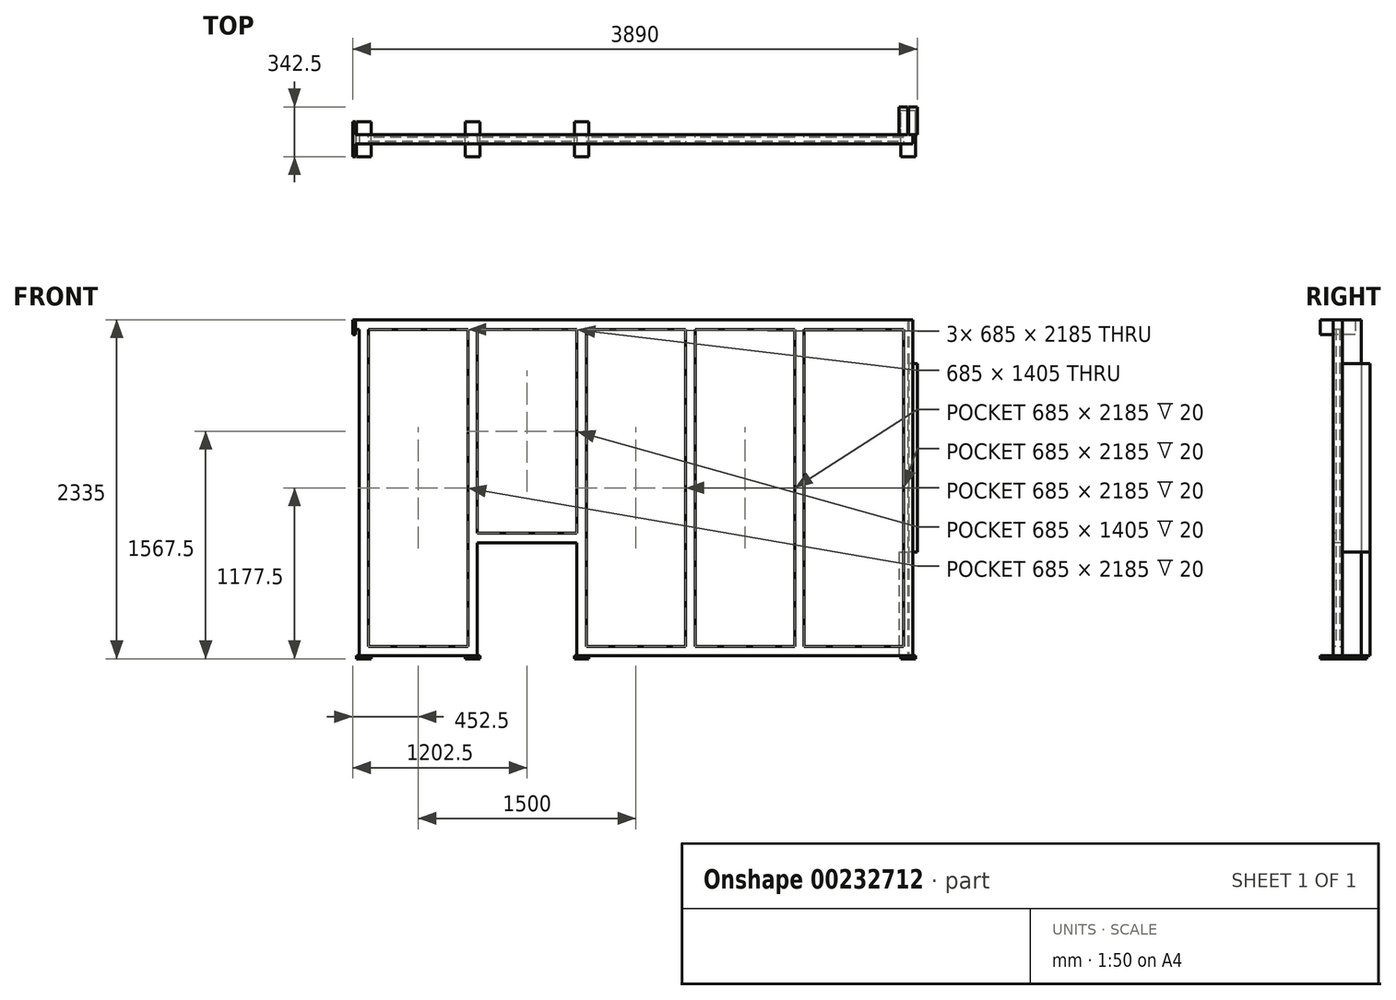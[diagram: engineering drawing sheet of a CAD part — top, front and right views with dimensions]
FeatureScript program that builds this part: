
annotation { "Feature Type Name" : "Feature", "Feature Type Description" : "" }
export const myFeature = defineFeature(function(context is Context, id is Id, definition is map)
    precondition{}
    {
        {
            var Q0;
            Q0=qCreatedBy(makeId("Front.planeOp"),FACE);
            var sketch = newSketch(context, id + "F0", { "sketchPlane" : qUnion([Q0])});
            skLineSegment(sketch, "E0.bottom", {"start": v(0, 0) * mm, "end": v(3815, 0) * mm});
            skLineSegment(sketch, "E0.top", {"start": v(0, 2315) * mm, "end": v(3815, 2315) * mm});
            skLineSegment(sketch, "E0.left", {"start": v(0, 0) * mm, "end": v(0, 2315) * mm});
            skLineSegment(sketch, "E0.right", {"start": v(3815, 0) * mm, "end": v(3815, 2315) * mm});
            skSolve(sketch);
        }
        {
            var Q0;
            Q0 = qSketchRegion(id + "F0", true);
            extrude(context, id + "F1", {"entities" : qUnion([Q0]), "oppositeDirection" : true, "depth" : 65 * mm});
        }
        {
            var Q0;
            Q0=makeQuery(id+"F1.opExtrude","CAP_FACE",FACE,{"disambiguationData":[OSD([sQuery(id+"F0.wireOp",EDGE,"E0.bottom"),sQuery(id+"F0.wireOp",EDGE,"E0.top"),sQuery(id+"F0.wireOp",EDGE,"E0.left"),sQuery(id+"F0.wireOp",EDGE,"E0.right")])],"isStart":true});
            var sketch = newSketch(context, id + "F2", { "sketchPlane" : qUnion([Q0])});
            skLineSegment(sketch, "E1.bottom", {"start": v(65, 65) * mm, "end": v(750, 65) * mm});
            skLineSegment(sketch, "E1.top", {"start": v(65, 2250) * mm, "end": v(750, 2250) * mm});
            skLineSegment(sketch, "E1.left", {"start": v(65, 65) * mm, "end": v(65, 2250) * mm});
            skLineSegment(sketch, "E1.right", {"start": v(750, 65) * mm, "end": v(750, 2250) * mm});
            skLineSegment(sketch, "E2.bottom", {"start": v(815, 2250) * mm, "end": v(1500, 2250) * mm});
            skLineSegment(sketch, "E2.top", {"start": v(815, 845) * mm, "end": v(1500, 845) * mm});
            skLineSegment(sketch, "E2.left", {"start": v(815, 2250) * mm, "end": v(815, 845) * mm});
            skLineSegment(sketch, "E2.right", {"start": v(1500, 2250) * mm, "end": v(1500, 845) * mm});
            skLineSegment(sketch, "E3.bottom", {"start": v(1565, 2250) * mm, "end": v(2250, 2250) * mm});
            skLineSegment(sketch, "E3.top", {"start": v(1565, 65) * mm, "end": v(2250, 65) * mm});
            skLineSegment(sketch, "E3.left", {"start": v(1565, 2250) * mm, "end": v(1565, 65) * mm});
            skLineSegment(sketch, "E3.right", {"start": v(2250, 2250) * mm, "end": v(2250, 65) * mm});
            skLineSegment(sketch, "E4.bottom", {"start": v(3065, 2250) * mm, "end": v(3750, 2250) * mm});
            skLineSegment(sketch, "E4.top", {"start": v(3065, 65) * mm, "end": v(3750, 65) * mm});
            skLineSegment(sketch, "E4.left", {"start": v(3065, 2250) * mm, "end": v(3065, 65) * mm});
            skLineSegment(sketch, "E4.right", {"start": v(3750, 2250) * mm, "end": v(3750, 65) * mm});
            skLineSegment(sketch, "E5.bottom", {"start": v(2315, 2250) * mm, "end": v(3000, 2250) * mm});
            skLineSegment(sketch, "E5.top", {"start": v(2315, 65) * mm, "end": v(3000, 65) * mm});
            skLineSegment(sketch, "E5.left", {"start": v(2315, 2250) * mm, "end": v(2315, 65) * mm});
            skLineSegment(sketch, "E5.right", {"start": v(3000, 2250) * mm, "end": v(3000, 65) * mm});
            skSolve(sketch);
        }
        {
            var Q0;
            Q0 = qSketchRegion(id + "F2", true);
            extrude(context, id + "F3", {"entities" : qUnion([Q0]), "operationType" : NewBodyOperationType.REMOVE, "oppositeDirection" : true, "depth" : 20 * mm});
        }
        {
            var Q0;
            {var subQ1=sQuery(id+"F0.wireOp",EDGE,"E0.left");var subQ3=sQuery(id+"F0.wireOp",EDGE,"E0.bottom");Q0=makeQuery(id+"F3.boolean.opBoolean","SPLIT",FACE,{"disambiguationData":[TD([makeQuery(id+"F1.opExtrude","SWEPT_FACE",FACE,{"disambiguationData":[OSD([subQ1])]})])],"derivedFrom":makeQuery(id+"F1.opExtrude","SWEPT_FACE",FACE,{"disambiguationData":[OSD([subQ3])]})});}
            var sketch = newSketch(context, id + "F4", { "sketchPlane" : qUnion([Q0])});
            skLineSegment(sketch, "E6.bottom", {"start": v(-17.5, 87.5) * mm, "end": v(82.5, 87.5) * mm});
            skLineSegment(sketch, "E6.top", {"start": v(-17.5, -152.5) * mm, "end": v(82.5, -152.5) * mm});
            skLineSegment(sketch, "E6.left", {"start": v(-17.5, 87.5) * mm, "end": v(-17.5, -152.5) * mm});
            skLineSegment(sketch, "E6.right", {"start": v(82.5, 87.5) * mm, "end": v(82.5, -152.5) * mm});
            skLineSegment(sketch, "E7.bottom", {"start": v(732.5, 87.5) * mm, "end": v(832.5, 87.5) * mm});
            skLineSegment(sketch, "E7.top", {"start": v(732.5, -152.5) * mm, "end": v(832.5, -152.5) * mm});
            skLineSegment(sketch, "E7.left", {"start": v(732.5, 87.5) * mm, "end": v(732.5, -152.5) * mm});
            skLineSegment(sketch, "E7.right", {"start": v(832.5, 87.5) * mm, "end": v(832.5, -152.5) * mm});
            skLineSegment(sketch, "E8.bottom", {"start": v(1482.5, 87.5) * mm, "end": v(1582.5, 87.5) * mm});
            skLineSegment(sketch, "E8.top", {"start": v(1482.5, -152.5) * mm, "end": v(1582.5, -152.5) * mm});
            skLineSegment(sketch, "E8.left", {"start": v(1482.5, 87.5) * mm, "end": v(1482.5, -152.5) * mm});
            skLineSegment(sketch, "E8.right", {"start": v(1582.5, 87.5) * mm, "end": v(1582.5, -152.5) * mm});
            skLineSegment(sketch, "E9.bottom", {"start": v(3732.5, 87.5) * mm, "end": v(3832.5, 87.5) * mm});
            skLineSegment(sketch, "E9.top", {"start": v(3732.5, -232.5) * mm, "end": v(3832.5, -232.5) * mm});
            skLineSegment(sketch, "E9.left", {"start": v(3732.5, 87.5) * mm, "end": v(3732.5, -232.5) * mm});
            skLineSegment(sketch, "E9.right", {"start": v(3832.5, 87.5) * mm, "end": v(3832.5, -232.5) * mm});
            skSolve(sketch);
        }
        {
            var Q0;
            Q0 = qSketchRegion(id + "F4", true);
            extrude(context, id + "F5", {"entities" : qUnion([Q0]), "operationType" : NewBodyOperationType.ADD, "depth" : 20 * mm});
        }
        {
            var Q0;
            Q0=makeQuery(id+"F1.opExtrude","SWEPT_FACE",FACE,{"disambiguationData":[OSD([sQuery(id+"F0.wireOp",EDGE,"E0.left")])]});
            var sketch = newSketch(context, id + "F6", { "sketchPlane" : qUnion([Q0])});
            skLineSegment(sketch, "E10.bottom", {"start": v(-65, 2315) * mm, "end": v(0, 2315) * mm});
            skLineSegment(sketch, "E10.top", {"start": v(-65, 2250) * mm, "end": v(0, 2250) * mm});
            skLineSegment(sketch, "E10.left", {"start": v(-65, 2315) * mm, "end": v(-65, 2250) * mm});
            skLineSegment(sketch, "E10.right", {"start": v(0, 2315) * mm, "end": v(0, 2250) * mm});
            skSolve(sketch);
        }
        {
            var Q0;
            Q0 = qSketchRegion(id + "F6", true);
            extrude(context, id + "F7", {"entities" : qUnion([Q0]), "operationType" : NewBodyOperationType.ADD, "depth" : 25 * mm});
        }
        {
            var Q0;
            Q0=makeQuery(id+"F7.opExtrude","CAP_FACE",FACE,{"disambiguationData":[OSD([sQuery(id+"F6.wireOp",EDGE,"E10.bottom"),sQuery(id+"F6.wireOp",EDGE,"E10.top"),sQuery(id+"F6.wireOp",EDGE,"E10.left"),sQuery(id+"F6.wireOp",EDGE,"E10.right")])],"isStart":false});
            var sketch = newSketch(context, id + "F8", { "sketchPlane" : qUnion([Q0])});
            skLineSegment(sketch, "E11.bottom", {"start": v(-152.5, 2315) * mm, "end": v(87.5, 2315) * mm});
            skLineSegment(sketch, "E11.top", {"start": v(-152.5, 2215) * mm, "end": v(87.5, 2215) * mm});
            skLineSegment(sketch, "E11.left", {"start": v(-152.5, 2315) * mm, "end": v(-152.5, 2215) * mm});
            skLineSegment(sketch, "E11.right", {"start": v(87.5, 2315) * mm, "end": v(87.5, 2215) * mm});
            skLineSegment(sketch, "E12", {"start": v(-32.5, 2315) * mm, "end": v(-32.5, 2215) * mm, "construction": true});
            skSolve(sketch);
        }
        {
            var Q0;
            Q0 = qSketchRegion(id + "F8", true);
            extrude(context, id + "F9", {"entities" : qUnion([Q0]), "operationType" : NewBodyOperationType.ADD, "depth" : 20 * mm});
        }
        {
            var Q0;
            Q0=makeQuery(id+"F7.boolean.opBoolean","MERGE",FACE,{"derivedFrom":[makeQuery(id+"F1.opExtrude","CAP_FACE",FACE,{"disambiguationData":[OSD([sQuery(id+"F0.wireOp",EDGE,"E0.bottom"),sQuery(id+"F0.wireOp",EDGE,"E0.top"),sQuery(id+"F0.wireOp",EDGE,"E0.left"),sQuery(id+"F0.wireOp",EDGE,"E0.right")])],"isStart":false}),makeQuery(id+"F7.opExtrude","SWEPT_FACE",FACE,{"disambiguationData":[OSD([sQuery(id+"F6.wireOp",EDGE,"E10.left")])]})]});
            var sketch = newSketch(context, id + "F10", { "sketchPlane" : qUnion([Q0])});
            skLineSegment(sketch, "E13.top", {"start": v(-3780, 0) * mm, "end": v(-3785, 0) * mm});
            skLineSegment(sketch, "E13.left", {"start": v(-3780, 2315) * mm, "end": v(-3780, 0) * mm});
            skLineSegment(sketch, "E13.right", {"start": v(-3785, 2315) * mm, "end": v(-3785, 0) * mm});
            skLineSegment(sketch, "E14", {"start": v(-3785, 2315) * mm, "end": v(-3780, 2315) * mm});
            skSolve(sketch);
        }
        {
            var Q0;
            Q0 = qSketchRegion(id + "F10", true);
            extrude(context, id + "F11", {"entities" : qUnion([Q0]), "operationType" : NewBodyOperationType.ADD, "depth" : 130 * mm});
        }
        {
            var Q0;
            Q0=makeQuery(id+"F11.opExtrude","SWEPT_FACE",FACE,{"disambiguationData":[OSD([sQuery(id+"F10.wireOp",EDGE,"E13.right")])]});
            var sketch = newSketch(context, id + "F12", { "sketchPlane" : qUnion([Q0])});
            skLineSegment(sketch, "E15.bottom", {"start": v(65, 2015) * mm, "end": v(255, 2015) * mm});
            skLineSegment(sketch, "E15.top", {"start": v(65, 715) * mm, "end": v(255, 715) * mm});
            skLineSegment(sketch, "E15.left", {"start": v(65, 2015) * mm, "end": v(65, 715) * mm});
            skLineSegment(sketch, "E16", {"start": v(255, 2015) * mm, "end": v(255, 715) * mm});
            skSolve(sketch);
        }
        {
            var Q0;
            Q0=makeQuery(id+"F12.imprint","IMPRINT",FACE,{"disambiguationData":[TD([[makeQuery(id+"F12.imprint","IMPRINT",EDGE,{"derivedFrom":sQuery(id+"F12.wireOp",EDGE,"E15.bottom")}),-1.0]])]});
            extrude(context, id + "F13", {"entities" : qUnion([Q0]), "operationType" : NewBodyOperationType.ADD, "depth" : 60 * mm});
        }
        {
            var Q0;
            Q0=makeQuery(id+"F11.opExtrude","SWEPT_FACE",FACE,{"disambiguationData":[OSD([sQuery(id+"F10.wireOp",EDGE,"E13.left")])]});
            var sketch = newSketch(context, id + "F14", { "sketchPlane" : qUnion([Q0])});
            skLineSegment(sketch, "E17.bottom", {"start": v(-255, 715) * mm, "end": v(-65, 715) * mm});
            skLineSegment(sketch, "E17.top", {"start": v(-255, 0) * mm, "end": v(-65, 0) * mm});
            skLineSegment(sketch, "E17.right", {"start": v(-65, 715) * mm, "end": v(-65, 0) * mm});
            skLineSegment(sketch, "E18", {"start": v(-255, 715) * mm, "end": v(-255, 0) * mm});
            skSolve(sketch);
        }
        {
            var Q0;
            Q0 = qSketchRegion(id + "F14", true);
            extrude(context, id + "F15", {"entities" : qUnion([Q0]), "operationType" : NewBodyOperationType.ADD, "depth" : 60 * mm});
        }
        {
            var Q0;
            Q0=makeQuery(id+"F7.boolean.opBoolean","MERGE",FACE,{"derivedFrom":[makeQuery(id+"F1.opExtrude","CAP_FACE",FACE,{"disambiguationData":[OSD([sQuery(id+"F0.wireOp",EDGE,"E0.bottom"),sQuery(id+"F0.wireOp",EDGE,"E0.top"),sQuery(id+"F0.wireOp",EDGE,"E0.left"),sQuery(id+"F0.wireOp",EDGE,"E0.right")])],"isStart":true}),makeQuery(id+"F7.opExtrude","SWEPT_FACE",FACE,{"disambiguationData":[OSD([sQuery(id+"F6.wireOp",EDGE,"E10.right")])]})]});
            var sketch = newSketch(context, id + "F16", { "sketchPlane" : qUnion([Q0])});
            skLineSegment(sketch, "E19.bottom", {"start": v(815, 780) * mm, "end": v(1500, 780) * mm});
            skLineSegment(sketch, "E19.top", {"start": v(815, 0) * mm, "end": v(1500, 0) * mm});
            skLineSegment(sketch, "E19.left", {"start": v(815, 780) * mm, "end": v(815, 0) * mm});
            skLineSegment(sketch, "E19.right", {"start": v(1500, 780) * mm, "end": v(1500, 0) * mm});
            skSolve(sketch);
        }
        {
            var Q0;
            Q0 = qSketchRegion(id + "F16", true);
            extrude(context, id + "F17", {"entities" : qUnion([Q0]), "operationType" : NewBodyOperationType.REMOVE, "endBound" : BoundingType.THROUGH_ALL, "oppositeDirection" : true, "depth" : 25 * mm});
        }
        {
            var Q0;
            {var subQ4=sQuery(id+"F0.wireOp",EDGE,"E0.bottom");var subQ6=sQuery(id+"F0.wireOp",EDGE,"E0.top");var subQ7=sQuery(id+"F0.wireOp",EDGE,"E0.left");Q0=makeQuery(id+"F11.boolean.opBoolean","SPLIT",FACE,{"disambiguationData":[TD([makeQuery(id+"F1.opExtrude","SWEPT_FACE",FACE,{"disambiguationData":[OSD([subQ4])]})])],"derivedFrom":makeQuery(id+"F7.boolean.opBoolean","MERGE",FACE,{"derivedFrom":[makeQuery(id+"F1.opExtrude","CAP_FACE",FACE,{"disambiguationData":[OSD([subQ4,subQ6,subQ7,sQuery(id+"F0.wireOp",EDGE,"E0.right")])],"isStart":false}),makeQuery(id+"F7.opExtrude","SWEPT_FACE",FACE,{"disambiguationData":[OSD([sQuery(id+"F6.wireOp",EDGE,"E10.left")])]})]})});}
            var sketch = newSketch(context, id + "F18", { "sketchPlane" : qUnion([Q0])});
            skLineSegment(sketch, "E20.bottom", {"start": v(-3750, 65) * mm, "end": v(-3065, 65) * mm});
            skLineSegment(sketch, "E20.top", {"start": v(-3750, 2250) * mm, "end": v(-3065, 2250) * mm});
            skLineSegment(sketch, "E20.left", {"start": v(-3750, 65) * mm, "end": v(-3750, 2250) * mm});
            skLineSegment(sketch, "E20.right", {"start": v(-3065, 65) * mm, "end": v(-3065, 2250) * mm});
            skLineSegment(sketch, "E21.bottom", {"start": v(-3000, 2250) * mm, "end": v(-2315, 2250) * mm});
            skLineSegment(sketch, "E21.top", {"start": v(-3000, 65) * mm, "end": v(-2315, 65) * mm});
            skLineSegment(sketch, "E21.left", {"start": v(-3000, 2250) * mm, "end": v(-3000, 65) * mm});
            skLineSegment(sketch, "E21.right", {"start": v(-2315, 2250) * mm, "end": v(-2315, 65) * mm});
            skLineSegment(sketch, "E22.bottom", {"start": v(-2250, 2250) * mm, "end": v(-1565, 2250) * mm});
            skLineSegment(sketch, "E22.top", {"start": v(-2250, 65) * mm, "end": v(-1565, 65) * mm});
            skLineSegment(sketch, "E22.left", {"start": v(-2250, 2250) * mm, "end": v(-2250, 65) * mm});
            skLineSegment(sketch, "E22.right", {"start": v(-1565, 2250) * mm, "end": v(-1565, 65) * mm});
            skLineSegment(sketch, "E23.bottom", {"start": v(-750, 2250) * mm, "end": v(-65, 2250) * mm});
            skLineSegment(sketch, "E23.top", {"start": v(-750, 65) * mm, "end": v(-65, 65) * mm});
            skLineSegment(sketch, "E23.left", {"start": v(-750, 2250) * mm, "end": v(-750, 65) * mm});
            skLineSegment(sketch, "E23.right", {"start": v(-65, 2250) * mm, "end": v(-65, 65) * mm});
            skLineSegment(sketch, "E24.bottom", {"start": v(-1500, 2250) * mm, "end": v(-815, 2250) * mm});
            skLineSegment(sketch, "E24.top", {"start": v(-1500, 845) * mm, "end": v(-815, 845) * mm});
            skLineSegment(sketch, "E24.left", {"start": v(-1500, 2250) * mm, "end": v(-1500, 845) * mm});
            skLineSegment(sketch, "E24.right", {"start": v(-815, 2250) * mm, "end": v(-815, 845) * mm});
            skSolve(sketch);
        }
        {
            var Q0;
            Q0 = qSketchRegion(id + "F18", true);
            extrude(context, id + "F19", {"entities" : qUnion([Q0]), "operationType" : NewBodyOperationType.REMOVE, "oppositeDirection" : true, "depth" : 20 * mm});
        }
    });
